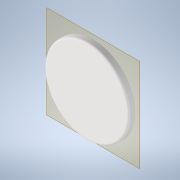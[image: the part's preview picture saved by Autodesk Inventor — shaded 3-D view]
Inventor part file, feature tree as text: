
AUTODESK INVENTOR PART (.ipt)
format: ipt  version: 2021.3 (Build 253353010, 353A)  size: 122,368 bytes
history: native  units: mm
features: plane x2, sketch x2, extrude x2, other x2, fillet x1, reference x1
ambient origin geometry x8: Origin, YZ Plane, XZ Plane, XY Plane, X Axis, Y Axis, Z Axis, Center Point
bodies: Volumenkörper1 (feature_tree)
feature tree (10):
  plane  "Arbeitsebene1"
  sketch  "Skizze1"  dims[d0=0.1mm d1=10.0mm d2=0.0mm]
  plane  "Arbeitsebene2"
  extrude  "Extrusion1"  Depth=10.0mm TaperAngle=0.0deg
  extrude  "Extrusion2"  Depth=1.0mm
  fillet  "Rundung1"  [1 undecoded]
  reference  "Referenz1"
  sketch  "Skizze2"  dims[d3=1.6mm d4=0.0mm d5=1.0mm]
  other  "Baugruppe1"
  other  "totmannschalter_grundplatte:1"
note: 1 required parameter value undecoded (feature->parameter linkage not recoverable at this tier; creation-order binding heuristic only, values carry confidence <= 0.55)
